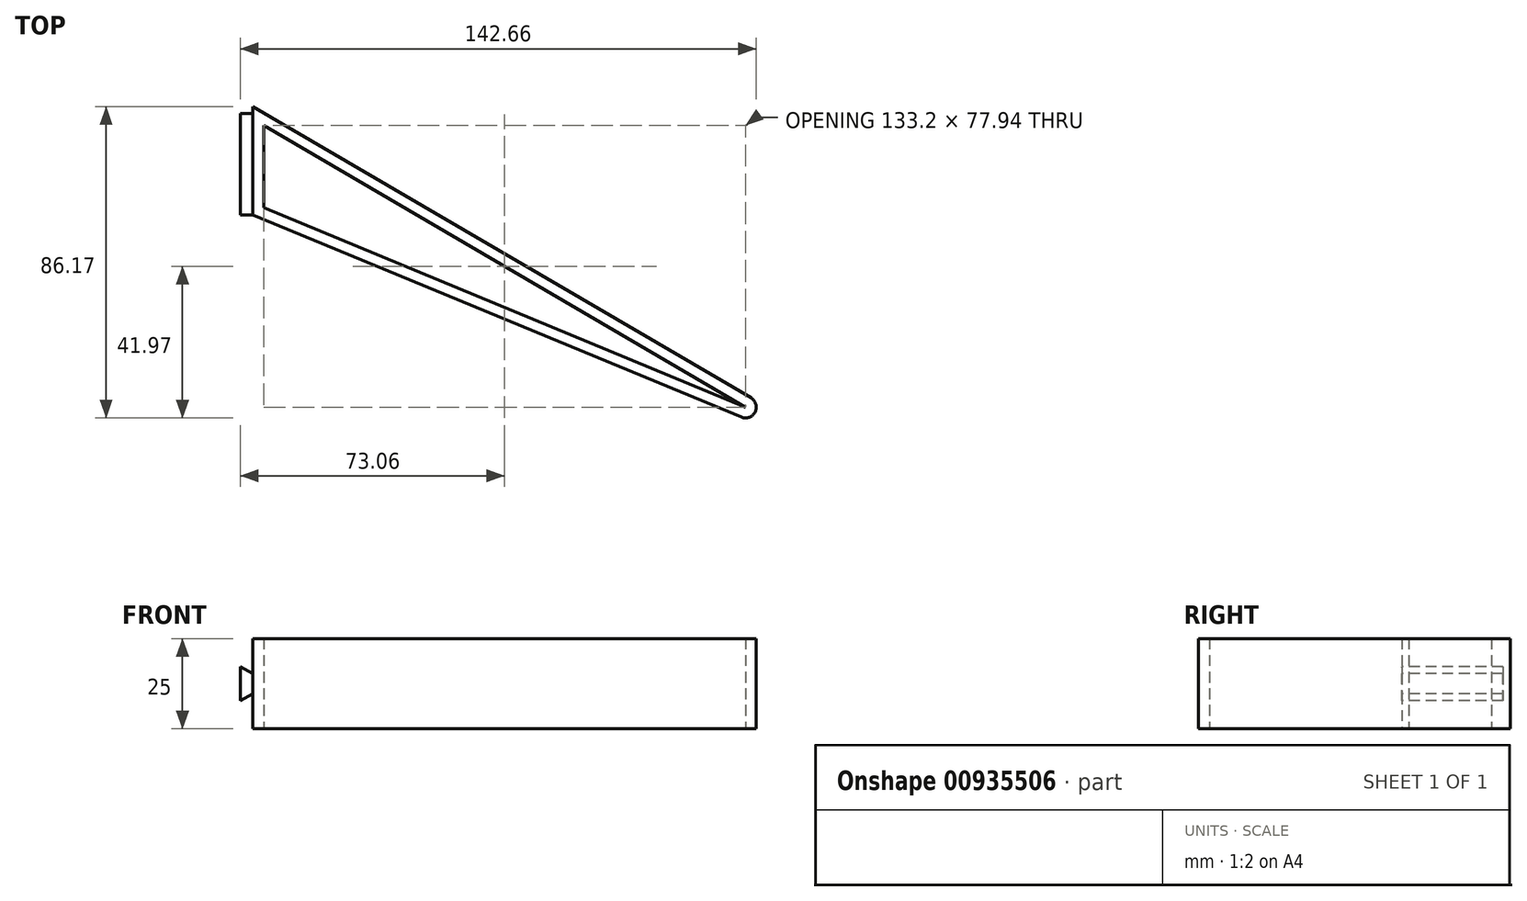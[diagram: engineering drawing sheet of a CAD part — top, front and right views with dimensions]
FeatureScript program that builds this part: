
annotation { "Feature Type Name" : "Feature", "Feature Type Description" : "" }
export const myFeature = defineFeature(function(context is Context, id is Id, definition is map)
    precondition{}
    {
        {
            var Q0;
            Q0=qCreatedBy(makeId("Top.planeOp"),FACE);
            var sketch = newSketch(context, id + "F0", { "sketchPlane" : qUnion([Q0])});
            skLineSegment(sketch, "E0", {"start": v(0, 0) * mm, "end": v(0, 30) * mm});
            skLineSegment(sketch, "E1", {"start": v(0, 0) * mm, "end": v(135.05, -55.94) * mm});
            skLineSegment(sketch, "E2", {"start": v(0, 30) * mm, "end": v(137.71, -50.58) * mm});
            skArc(sketch, "E3", {"start": v(135.05, -55.94) * mm, "mid": v(138.89, -54.5) * mm, "end": v(137.71, -50.58) * mm});
            skPoint(sketch, "E4.orphan", {"position": v(175.54, -72.7) * mm});
            skLineSegment(sketch, "E5.0", {"start": v(3, 24.77) * mm, "end": v(136.2, -53.17) * mm});
            skLineSegment(sketch, "E5.1", {"start": v(3, 2) * mm, "end": v(3, 24.77) * mm});
            skLineSegment(sketch, "E5.2", {"start": v(3, 2) * mm, "end": v(136.2, -53.17) * mm});
            skSolve(sketch);
        }
        {
            var Q0;
            Q0=makeQuery(id+"F0.imprint","IMPRINT",FACE,{"disambiguationData":[TD([[makeQuery(id+"F0.imprint","IMPRINT",EDGE,{"derivedFrom":sQuery(id+"F0.wireOp",EDGE,"E0")}),-1.0]])]});
            extrude(context, id + "F1", {"entities" : qUnion([Q0]), "depth" : 25 * mm, "offsetDistance" : 25 * mm});
        }
        {
            var Q0;
            Q0=qCreatedBy(makeId("Front.planeOp"),FACE);
            var sketch = newSketch(context, id + "F2", { "sketchPlane" : qUnion([Q0])});
            skLineSegment(sketch, "E6", {"start": v(0, 15.25) * mm, "end": v(0, 9.75) * mm});
            skLineSegment(sketch, "E7", {"start": v(0, 9.75) * mm, "end": v(-3.46, 7.75) * mm});
            skLineSegment(sketch, "E8", {"start": v(-3.46, 7.75) * mm, "end": v(-3.46, 17.25) * mm});
            skLineSegment(sketch, "E9", {"start": v(-3.46, 17.25) * mm, "end": v(0, 15.25) * mm});
            skLineSegment(sketch, "E10", {"start": v(0, 9.75) * mm, "end": v(0, 0) * mm, "construction": true});
            skLineSegment(sketch, "E11", {"start": v(0, 15.25) * mm, "end": v(0, 25) * mm, "construction": true});
            skSolve(sketch);
        }
        {
            var Q0;
            Q0=makeQuery(id+"F2.imprint","IMPRINT",FACE,{"disambiguationData":[TD([[makeQuery(id+"F2.imprint","IMPRINT",EDGE,{"derivedFrom":sQuery(id+"F2.wireOp",EDGE,"E6")}),-1.0]])]});
            extrude(context, id + "F3", {"entities" : qUnion([Q0]), "operationType" : NewBodyOperationType.ADD, "oppositeDirection" : true, "depth" : 28 * mm, "offsetDistance" : 25 * mm});
        }
    });
